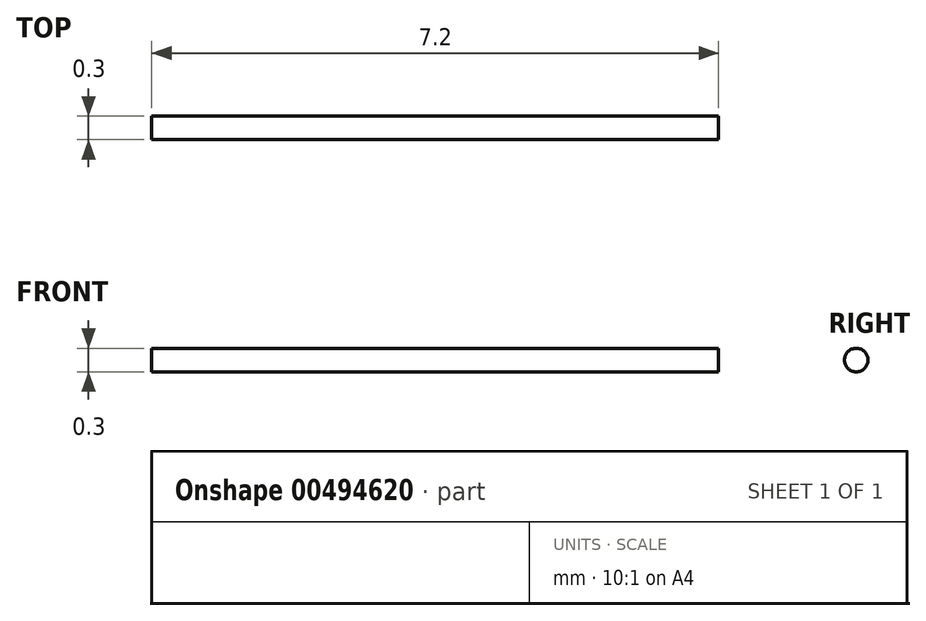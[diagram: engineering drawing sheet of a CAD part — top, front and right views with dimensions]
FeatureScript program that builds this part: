
annotation { "Feature Type Name" : "Feature", "Feature Type Description" : "" }
export const myFeature = defineFeature(function(context is Context, id is Id, definition is map)
    precondition{}
    {
        {
            var Q0;
            Q0=qCreatedBy(makeId("Right.planeOp"),FACE);
            var sketch = newSketch(context, id + "F0", { "sketchPlane" : qUnion([Q0])});
            skCircle(sketch, "E0", {"center": v(0, 0) * mm, "radius": 0.15 * mm});
            skSolve(sketch);
        }
        {
            var Q0;
            Q0=makeQuery(id+"F0.imprint","IMPRINT",FACE,{"disambiguationData":[TD([[makeQuery(id+"F0.imprint","IMPRINT",EDGE,{"derivedFrom":sQuery(id+"F0.wireOp",EDGE,"E0")}),1.0]])]});
            extrude(context, id + "F1", {"entities" : qUnion([Q0]), "depth" : 7.2 * mm, "offsetDistance" : 25 * mm});
        }
    });
